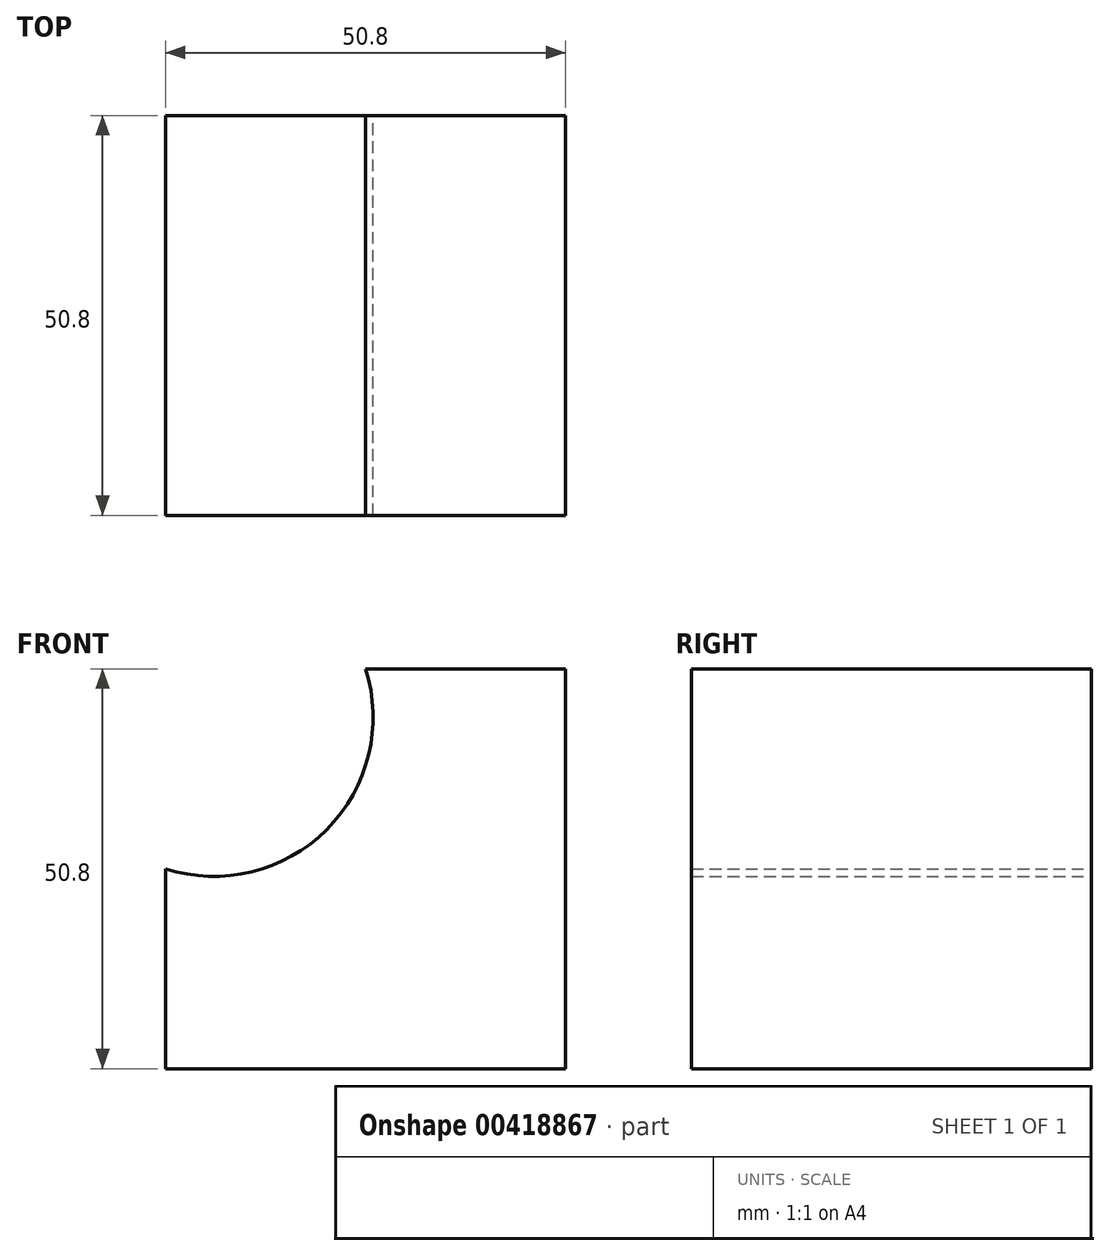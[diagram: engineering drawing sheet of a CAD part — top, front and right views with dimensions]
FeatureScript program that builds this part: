
annotation { "Feature Type Name" : "Feature", "Feature Type Description" : "" }
export const myFeature = defineFeature(function(context is Context, id is Id, definition is map)
    precondition{}
    {
        {
            var Q0;
            Q0=qCreatedBy(makeId("Front.planeOp"),FACE);
            var sketch = newSketch(context, id + "F0", { "sketchPlane" : qUnion([Q0])});
            skLineSegment(sketch, "E0", {"start": v(0, 0) * mm, "end": v(0, 50.8) * mm});
            skLineSegment(sketch, "E1", {"start": v(0, 0) * mm, "end": v(-50.8, 0) * mm});
            skLineSegment(sketch, "E2", {"start": v(0, 50.8) * mm, "end": v(-25.4, 50.8) * mm});
            skLineSegment(sketch, "E3", {"start": v(-50.8, 0) * mm, "end": v(-50.8, 25.4) * mm});
            skArc(sketch, "E4", {"start": v(-50.8, 25.4) * mm, "mid": v(-30.36, 30.36) * mm, "end": v(-25.4, 50.8) * mm});
            skSolve(sketch);
        }
        {
            var Q0;
            Q0 = qSketchRegion(id + "F0", true);
            extrude(context, id + "F1", {"entities" : qUnion([Q0]), "depth" : 50.8 * mm});
        }
    });
